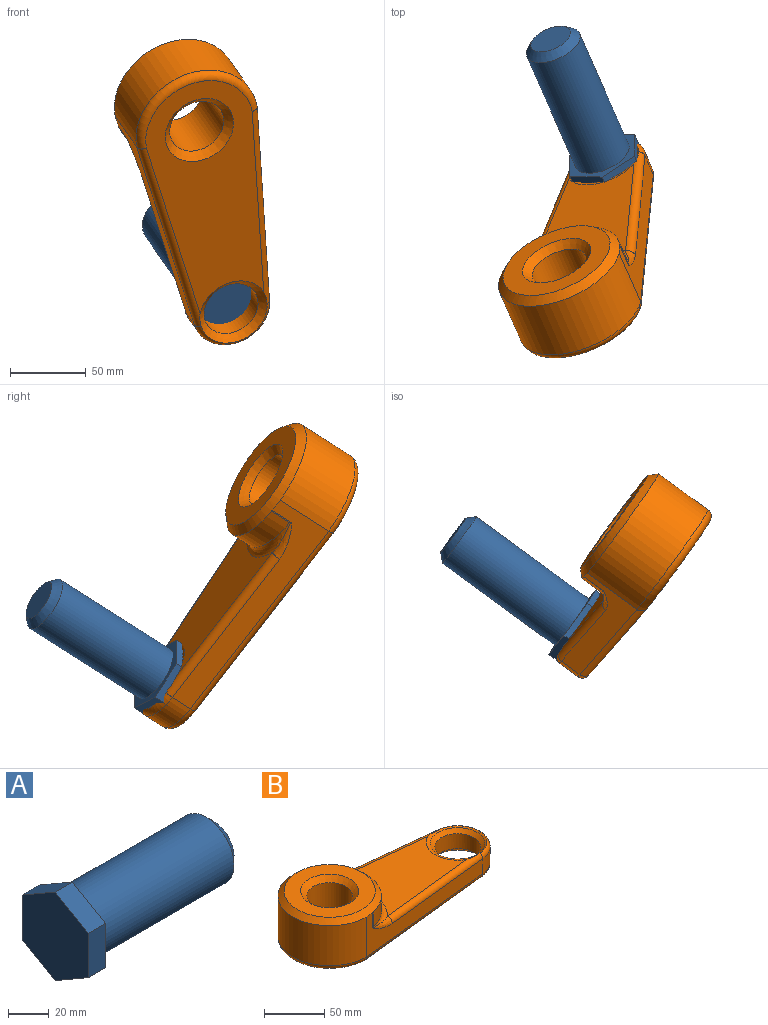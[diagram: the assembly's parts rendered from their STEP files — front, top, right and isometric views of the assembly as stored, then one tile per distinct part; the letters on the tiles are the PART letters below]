
ASSEMBLY  parts=2 mates=1
PART A: 11 faces, bbox 109.5x45.8x52.9 mm
  f0: plane 22.92x13.23mm, normal (0,0.5,-0.87), area 316.3mm2, adj f1,f5,f6,f7
  f1: plane 26.47x11.95mm, normal (0,1,0), area 316.3mm2, adj f0,f2,f6,f7
  f2: plane 22.92x13.23mm, normal (0,0.5,0.87), area 316.3mm2, adj f1,f3,f6,f7
  f3: plane 22.92x13.23mm, normal (0,-0.5,0.87), area 316.3mm2, adj f2,f4,f6,f7
  f4: plane 26.47x11.95mm, normal (0,-1,0), area 316.3mm2, adj f3,f5,f6,f7
  f5: plane 22.92x13.23mm, normal (0,-0.5,-0.87), area 316.3mm2, adj f0,f4,f6,f7
  f6: plane 52.94x45.84mm, normal (-1,0,0), area 1820.1mm2, adj f0,f1,f2,f3,f4,f5
  f7: plane 52.94x45.84mm, normal (1,0,0), area 680mm2, adj f0,f1,f2,f3,f4,f5,f8
  f8: cylinder r=19.05mm len=92.44mm, axis (-1,0,0), area 11064.5mm2, adj f7,f10
  f9: plane 27.94x27.94mm, normal (1,0,0), area 613.1mm2, adj f10
  f10: cone r=13.97mm half-angle=45deg, axis (-1,0,0), area 745.3mm2, adj f8,f9
PART B: 28 faces, bbox 229x109.1x50.8 mm
  f0: plane 104.32x68.52mm, normal (0,0,1), area 4851.9mm2, adj f14,f17,f19,f20
  f1: plane 153.06x40.88mm, normal (0.11,0.99,0), area 2652.1mm2, adj f2,f5,f13,f19,f21,f22,f26
  f2: cylinder r=42.94mm len=85.87mm, axis (0,0,-1), area 5482mm2, adj f1,f3,f13,f24
  f3: plane 153.07x40.88mm, normal (0.11,-0.99,0), area 2652.1mm2, adj f2,f5,f13,f14,f15,f18,f23
  f4: cylinder r=19.05mm len=40.64mm, axis (0,0,-1), area 4864.4mm2, adj f11,f12
  f5: cylinder r=26.84mm len=53.39mm, axis (0,0,-1), area 1198.8mm2, adj f1,f3,f16,f25
  f6: cylinder r=19.05mm len=38.1mm, axis (0,0,-1), area 1824.1mm2, adj f10,f27
  f7: plane 180.02x75.71mm, normal (0,0,-1), area 8500.3mm2, adj f12,f23,f24,f26,f27
  f8: cylinder r=42.94mm len=83.84mm, axis (0,0,-1), area 1770mm2, adj f13,f15,f20,f22
  f9: plane 75.71x75.71mm, normal (0,0,1), area 2673.2mm2, adj f11,f13
  f10: cone r=19.05mm half-angle=45deg, axis (0,0,1), area 665.4mm2, adj f6,f17
  f11: cone r=19.05mm half-angle=45deg, axis (0,0,1), area 974.6mm2, adj f4,f9
  f12: cone r=24.13mm half-angle=45deg, axis (0,0,-1), area 974.6mm2, adj f4,f7
  f13: cone r=37.86mm half-angle=45deg, axis (0,0,-1), area 1819.4mm2, adj f1,f2,f3,f8,f9,f15,f22
  f14: cylinder r=5.08mm len=119.42mm, axis (-0.99,-0.11,0), area 937mm2, adj f0,f3,f16,f17,f18
  f15: cylinder r=5.08mm len=15.27mm, axis (0,0,-1), area 8.7mm2, adj f3,f8,f13,f18
  f16: torus R=21.76mm, axis (0,0,1), area 429.2mm2, adj f5,f14,f17,f19
  f17: torus R=26.23mm, axis (0,0,1), area 405.1mm2, adj f0,f10,f14,f16,f19
  f18: bspline ~26.19x10.33mm, area 115.8mm2, adj f3,f14,f15,f20
  f19: cylinder r=5.08mm len=119.42mm, axis (0.99,-0.11,0), area 937mm2, adj f0,f1,f16,f17,f21
  f20: torus R=48.02mm, axis (0,0,1), area 763.3mm2, adj f0,f8,f18,f21
  f21: bspline ~27.57x10.45mm, area 115.8mm2, adj f1,f19,f20,f22
  f22: cylinder r=5.08mm len=15.27mm, axis (0,0,-1), area 8.7mm2, adj f1,f8,f13,f21
  f23: cylinder r=5.08mm len=153.6mm, axis (0.99,0.11,0), area 1216.6mm2, adj f3,f7,f24,f25,f27
  f24: torus R=37.86mm, axis (0,0,1), area 1027.9mm2, adj f2,f7,f23,f26
  f25: torus R=21.76mm, axis (0,0,1), area 449.7mm2, adj f5,f23,f26,f27
  f26: cylinder r=5.08mm len=153.6mm, axis (-0.99,0.11,0), area 1216.6mm2, adj f1,f7,f24,f25,f27
  f27: cone r=24.13mm half-angle=45deg, axis (0,0,-1), area 929.2mm2, adj f6,f7,f23,f25,f26
PLACE A rot(axis=(-0.55,-0.8,-0.23),161.7deg) t=(43.81,46.77,-128.43)mm
PLACE B rot(axis=(-0.58,0.24,0.78),106deg) t=(31.36,-63.09,-22.53)mm
MATE cylindrical A.f8 <-> B.f6  axis (-0.35,0.79,0.5) through (9.67,123.94,-79.56)mm
